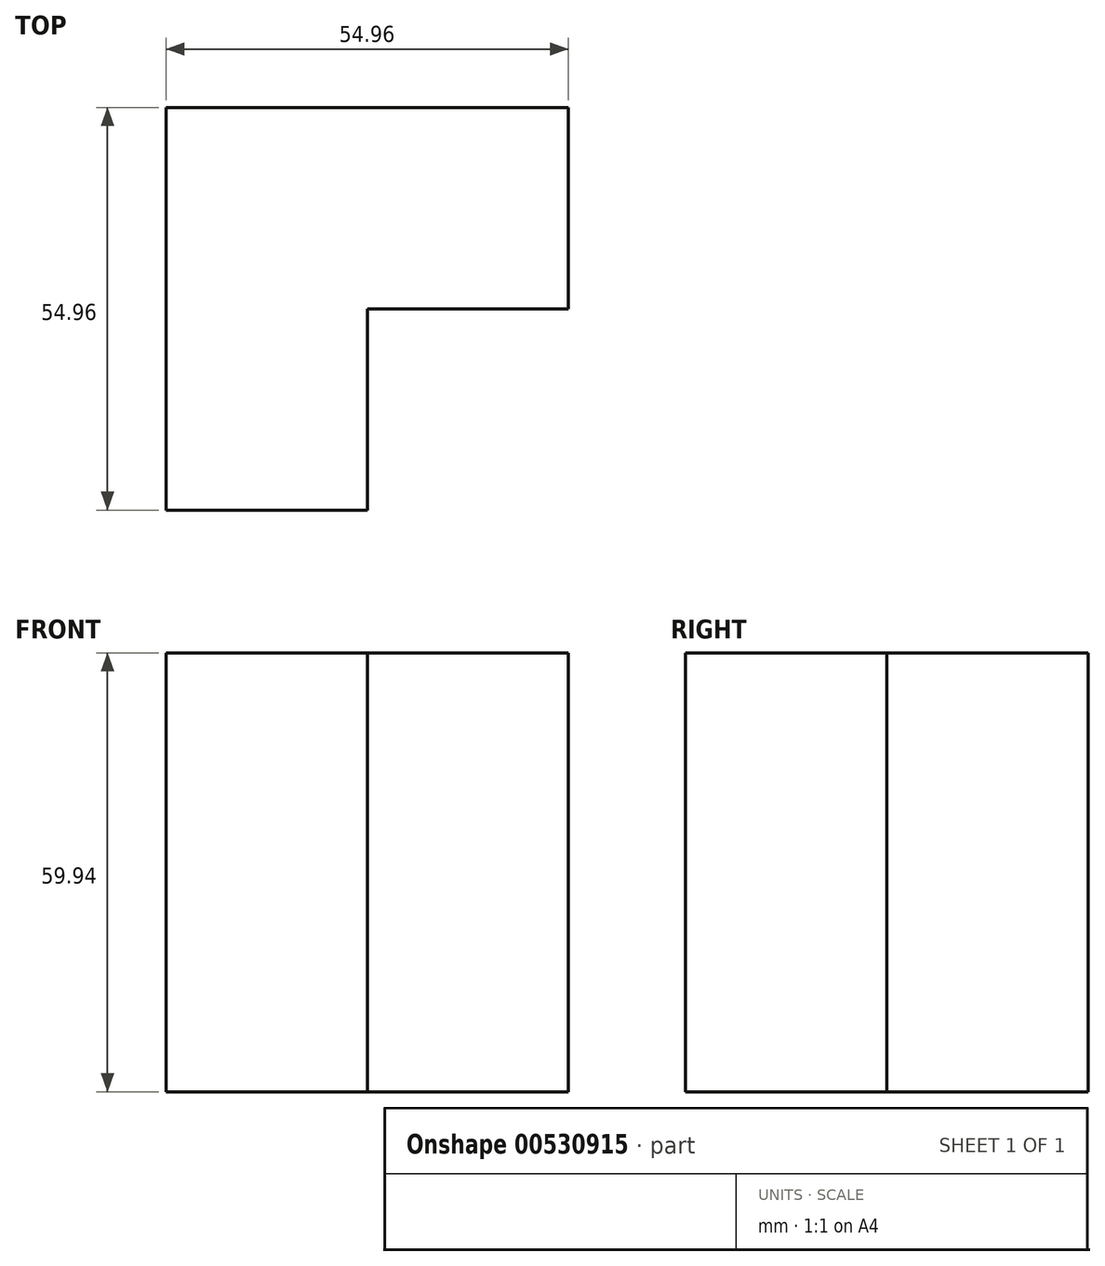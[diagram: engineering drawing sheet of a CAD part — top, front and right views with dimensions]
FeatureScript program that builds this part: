
annotation { "Feature Type Name" : "Feature", "Feature Type Description" : "" }
export const myFeature = defineFeature(function(context is Context, id is Id, definition is map)
    precondition{}
    {
        {
            var Q0;
            Q0=qCreatedBy(makeId("Top.planeOp"),FACE);
            var sketch = newSketch(context, id + "F0", { "sketchPlane" : qUnion([Q0])});
            skLineSegment(sketch, "E0.bottom", {"start": v(0, 0) * mm, "end": v(54.96, 0) * mm});
            skLineSegment(sketch, "E0.top", {"start": v(0, -54.96) * mm, "end": v(27.48, -54.96) * mm});
            skLineSegment(sketch, "E0.left", {"start": v(0, 0) * mm, "end": v(0, -54.96) * mm});
            skLineSegment(sketch, "E0.right", {"start": v(54.96, 0) * mm, "end": v(54.96, -27.48) * mm});
            skLineSegment(sketch, "E1", {"start": v(54.96, -27.48) * mm, "end": v(27.48, -27.48) * mm});
            skPoint(sketch, "E1.endSnap0", {"position": v(54.96, -27.48) * mm});
            skLineSegment(sketch, "E2", {"start": v(27.48, -27.48) * mm, "end": v(27.48, -54.96) * mm});
            skPoint(sketch, "E3.orphan", {"position": v(54.96, -54.96) * mm});
            skLineSegment(sketch, "E4", {"start": v(-15.59, 40.3) * mm, "end": v(46.15, 40.3) * mm});
            skSolve(sketch);
        }
        {
            var Q0;
            Q0 = qSketchRegion(id + "F0", true);
            extrude(context, id + "F1", {"entities" : qUnion([Q0]), "depth" : 59.94 * mm, "offsetDistance" : 25.4 * mm});
        }
    });
